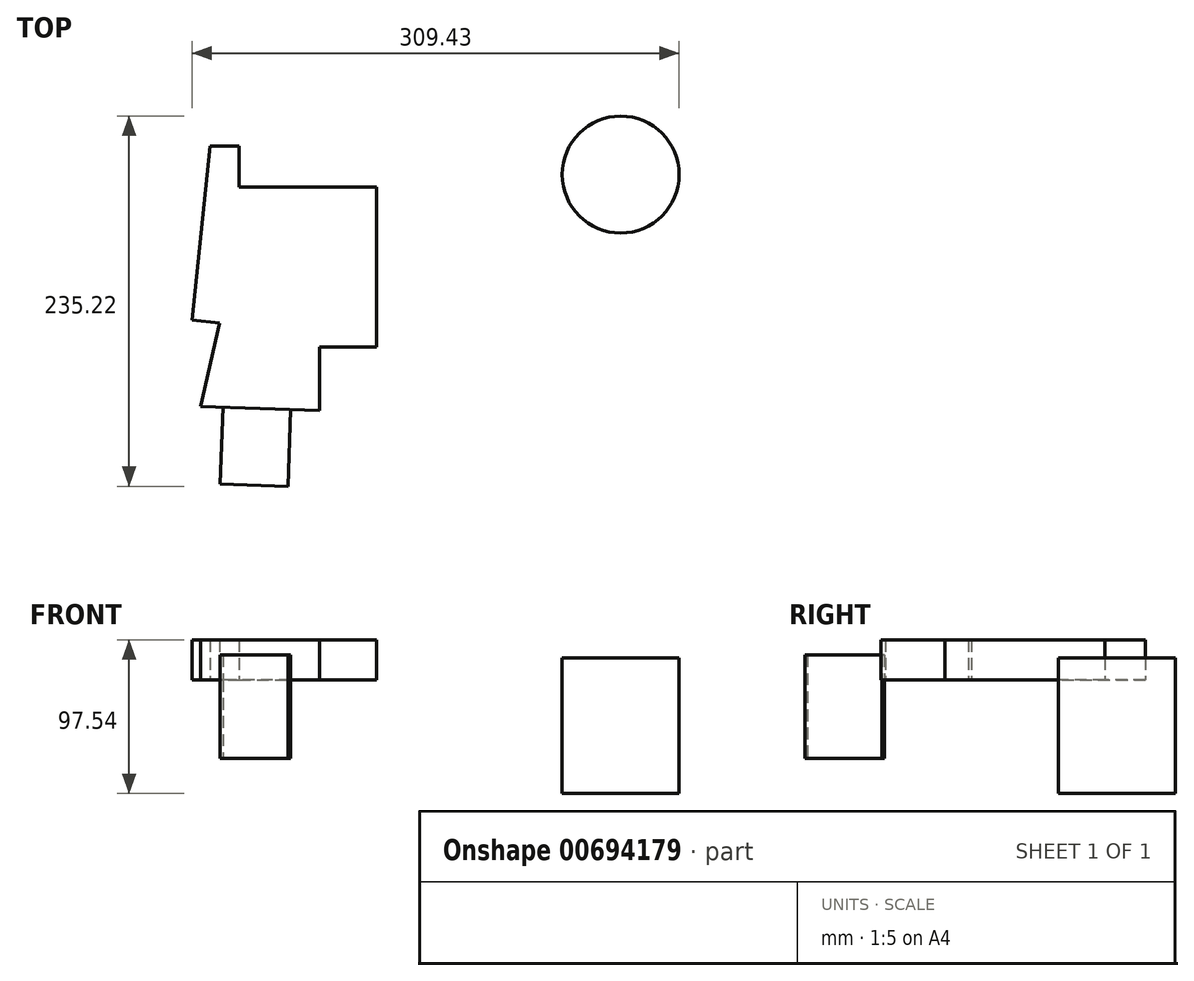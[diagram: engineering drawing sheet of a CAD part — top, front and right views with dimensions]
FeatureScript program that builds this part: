
annotation { "Feature Type Name" : "Feature", "Feature Type Description" : "" }
export const myFeature = defineFeature(function(context is Context, id is Id, definition is map)
    precondition{}
    {
        {
            var Q0;
            Q0=qCreatedBy(makeId("Top.planeOp"),FACE);
            var sketch = newSketch(context, id + "F0", { "sketchPlane" : qUnion([Q0])});
            skLineSegment(sketch, "E0", {"start": v(-120.43, -26.36) * mm, "end": v(-108.9, 84.1) * mm});
            skLineSegment(sketch, "E1", {"start": v(-108.9, 84.1) * mm, "end": v(-90.63, 84.1) * mm});
            skLineSegment(sketch, "E2", {"start": v(-90.63, 84.1) * mm, "end": v(-90.63, 58.31) * mm});
            skLineSegment(sketch, "E3", {"start": v(-90.63, 58.31) * mm, "end": v(-3.25, 58.31) * mm});
            skLineSegment(sketch, "E4", {"start": v(-3.25, 58.31) * mm, "end": v(-3.25, -43.31) * mm});
            skLineSegment(sketch, "E5", {"start": v(-3.25, -43.31) * mm, "end": v(-39.5, -43.31) * mm});
            skLineSegment(sketch, "E6", {"start": v(-39.5, -43.31) * mm, "end": v(-39.5, -83.91) * mm});
            skLineSegment(sketch, "E7", {"start": v(-39.5, -83.91) * mm, "end": v(-115.06, -81.06) * mm});
            skLineSegment(sketch, "E8", {"start": v(-115.06, -81.06) * mm, "end": v(-103, -28.18) * mm});
            skLineSegment(sketch, "E9", {"start": v(-103, -28.18) * mm, "end": v(-120.43, -26.36) * mm});
            skSolve(sketch);
        }
        {
            var Q0;
            Q0=makeQuery(id+"F0.imprint","IMPRINT",FACE,{"disambiguationData":[TD([[makeQuery(id+"F0.imprint","IMPRINT",EDGE,{"derivedFrom":sQuery(id+"F0.wireOp",EDGE,"E0")}),-1.0]])]});
            extrude(context, id + "F1", {"entities" : qUnion([Q0]), "depth" : 25.4 * mm, "offsetDistance" : 25.4 * mm});
        }
        {
            var Q0;
            Q0=qCreatedBy(makeId("Top.planeOp"),FACE);
            var sketch = newSketch(context, id + "F2", { "sketchPlane" : qUnion([Q0])});
            skCircle(sketch, "E10", {"center": v(74.64, 18.87) * mm, "radius": 37.15 * mm});
            skSolve(sketch);
        }
        {
            var Q0;
            Q0=makeQuery(id+"F2.imprint","IMPRINT",FACE,{"disambiguationData":[TD([[makeQuery(id+"F2.imprint","IMPRINT",EDGE,{"derivedFrom":sQuery(id+"F2.wireOp",EDGE,"E10")}),1.0]])]});
            extrude(context, id + "F3", {"entities" : qUnion([Q0]), "depth" : 86.1 * mm, "offsetDistance" : 25.4 * mm});
        }
        {
            var Q0;
            Q0=makeQuery(id+"F1.opExtrude","SWEPT_FACE",FACE,{"disambiguationData":[OSD([sQuery(id+"F0.wireOp",EDGE,"E7")])]});
            var sketch = newSketch(context, id + "F4", { "sketchPlane" : qUnion([Q0])});
            skLineSegment(sketch, "E11.bottom", {"start": v(-97.44, 15.73) * mm, "end": v(-54.5, 15.73) * mm});
            skLineSegment(sketch, "E11.top", {"start": v(-97.44, -49.88) * mm, "end": v(-54.5, -49.88) * mm});
            skLineSegment(sketch, "E11.left", {"start": v(-97.44, 15.73) * mm, "end": v(-97.44, -49.88) * mm});
            skLineSegment(sketch, "E11.right", {"start": v(-54.5, 15.73) * mm, "end": v(-54.5, -49.88) * mm});
            skSolve(sketch);
        }
        {
            var Q0;
            {var subQ0=sQuery(id+"F4.wireOp",EDGE,"E11.bottom");Q0=makeQuery(id+"F4.imprint","IMPRINT",FACE,{"disambiguationData":[TD([[makeQuery(id+"F4.imprint","IMPRINT",EDGE,{"derivedFrom":subQ0}),-1.0]])]});}
            var Q1;
            {var subQ0=sQuery(id+"F4.wireOp",EDGE,"E11.top");Q1=makeQuery(id+"F4.imprint","IMPRINT",FACE,{"disambiguationData":[TD([[makeQuery(id+"F4.imprint","IMPRINT",EDGE,{"derivedFrom":subQ0}),1.0]])]});}
            extrude(context, id + "F5", {"entities" : qUnion([Q0, Q1]), "operationType" : NewBodyOperationType.ADD, "depth" : 48.77 * mm, "offsetDistance" : 25.4 * mm});
        }
        {
            var Q0;
            Q0=makeQuery(id+"F1.opExtrude","SWEPT_BODY",BODY,{"disambiguationData":[OSD([sQuery(id+"F0.wireOp",EDGE,"E0"),sQuery(id+"F0.wireOp",EDGE,"E1"),sQuery(id+"F0.wireOp",EDGE,"E2"),sQuery(id+"F0.wireOp",EDGE,"E3"),sQuery(id+"F0.wireOp",EDGE,"E4"),sQuery(id+"F0.wireOp",EDGE,"E5"),sQuery(id+"F0.wireOp",EDGE,"E6"),sQuery(id+"F0.wireOp",EDGE,"E7"),sQuery(id+"F0.wireOp",EDGE,"E8"),sQuery(id+"F0.wireOp",EDGE,"E9")])]});
            transform(context, id + "F6", {"entities" : qUnion([Q0]), "transformType" : TransformType.TRANSLATION_3D, "dx" : -77.22 * mm, "dy" : -47.24 * mm, "dz" : 72.14 * mm, "makeCopy" : false});
        }
    });
